# Revit family: HerzCon-Fan-coils and terminal units connection 65mm LF,MF
name_source: partatom
category: Rohrzubehör
units: mm (PartAtom-declared; Revit-internal decimal feet)

## family parameters
Arbeitsebenenbasiert = Nein
Beim Laden mit Abzugskörper schneiden = Nein
Bemaßung runder Anschluss = Durchmesser verwenden
Gemeinsam genutzt = Nein
Immer vertikal = Ja
OmniClass-Nummer = 23.65.55.14
OmniClass-Titel = Valves for Liquid Services
Teiletyp = Unterbricht

## types (2) — shared parameters
Application = HerzCON has been designed to give a simple connection to fan-coils, or other terminal units, and utilises the HERZ 4006 SMART Pressure Independent Balancing Control Valve with HERZ multifunctional ball valve and a HERZ strainer with HERZ drain valve 2512.
On/off or modulating 0 – 10 V DC actuators can be fitted and integrated to a BMS if required.
The unit allows pressure independent control ensuring full stroke regardless of pressure fluctuations, while guaranteeing a constant flow rate to the terminal unit maximising energy efficiency for the system.
The HerzCON unit also permits flushing and isolating operations to be undertaken.
This means there is no product differentiation between heating and chilled, one unit does both applications.
The drain cock fitted to the strainer allows flushing without the need to remove the strainer basket and also allows the strainer basket to be cleaned in-situ.
Body = dezincification-resistant brass
D01 = 13 mm
D02 = 16.5 mm  [stored 0.0541339 ft]
D03 = 14.5 mm  [stored 0.0475722 ft]
D04 = 10 mm  [stored 0.0328084 ft]
D05 = 16.75 mm  [stored 0.0549541 ft]
D06 = 20.5 mm  [stored 0.0672572 ft]
D07 = 7.5 mm  [stored 0.0246063 ft]
D10 = 13.5 mm  [stored 0.0442913 ft]
D11 = 10.75 mm  [stored 0.035269 ft]
D12 = 12 mm  [stored 0.0393701 ft]
H01 = 19.5 mm  [stored 0.0639764 ft]
H02 = 26.55 mm  [stored 0.0871063 ft]
H03 = 26 mm
H04 = 2.5 mm  [stored 0.0082021 ft]
H05 = 18.5 mm  [stored 0.0606955 ft]
H06 = 8 mm  [stored 0.0262467 ft]
H07 = 27.8 mm  [stored 0.0912073 ft]
H08 = 2 mm  [stored 0.00656168 ft]
H09 = 7.2 mm  [stored 0.023622 ft]
H10 = 2 mm  [stored 0.00656168 ft]
H11 = 58.8 mm  [stored 0.192913 ft]
H15 = 75 mm
H16 = 34 mm
Hersteller = HERZ Armaturen Ges.m.b.H.
ISO01 = 181 mm
ISO02 = 176 mm
ISO03 = 15 mm  [stored 0.0492126 ft]
ISO04 = 47 mm  [stored 0.154199 ft]
ISO05 = 49 mm  [stored 0.160761 ft]
ISO06 = 114 mm  [stored 0.374016 ft]
ISO07 = -47 mm  [stored -0.154199 ft]
ISO08 = 134 mm  [stored 0.439633 ft]
ISOH01 = 50 mm  [stored 0.164042 ft]
ISOH02 = -38 mm  [stored -0.124672 ft]
ISOR01 = 17.5 mm  [stored 0.0574147 ft]
Insulation box = EPP, water vapour impermeable, black
KombiH04 = 23.6 mm  [stored 0.0774278 ft]
L01 = 6 mm  [stored 0.019685 ft]
L02 = 5 mm  [stored 0.0164042 ft]
L03 = 7 mm  [stored 0.0229659 ft]
Lift = 4 mm
Max. operating pressure = 2500000.0 Pa
Max. operating temperature = 130 °C
Medium = Water purity in accordance with the ÖNORM H 5195 and VDI 2035 standards.
Ethylene and propylene glycol can be mixed to a ratio of 25 - 50 vol. [%].
Membranes and O-rings = EPDM
Min. operating temperature = -20 °C
SCRNCODE = 05;04;04
SCRNSEQ = ARM;TYP_ARM="DURR";02
SFD02 = 18 mm  [stored 0.0590551 ft]
SFD03 = 13.5 mm  [stored 0.0442913 ft]
SFH03 = 32.5 mm  [stored 0.106627 ft]
SFH04 = 26 mm
SFH05 = 19.5 mm  [stored 0.0639764 ft]
SFL01 = 17 mm  [stored 0.0557743 ft]
SFL02 = 12.4 mm
SFR01 = 16.5 mm  [stored 0.0541339 ft]
SFR02 = 5.5 mm  [stored 0.0180446 ft]
URL = www.herzvalves.com
WI00 = 45.00°
WI01 = 120.00°

## type names (no varying parameters)
- DN15 LF
- DN15 MF

note: [stored X ft] marks values corroborated as IEEE doubles in the binary element streams (Revit-internal decimal feet)
